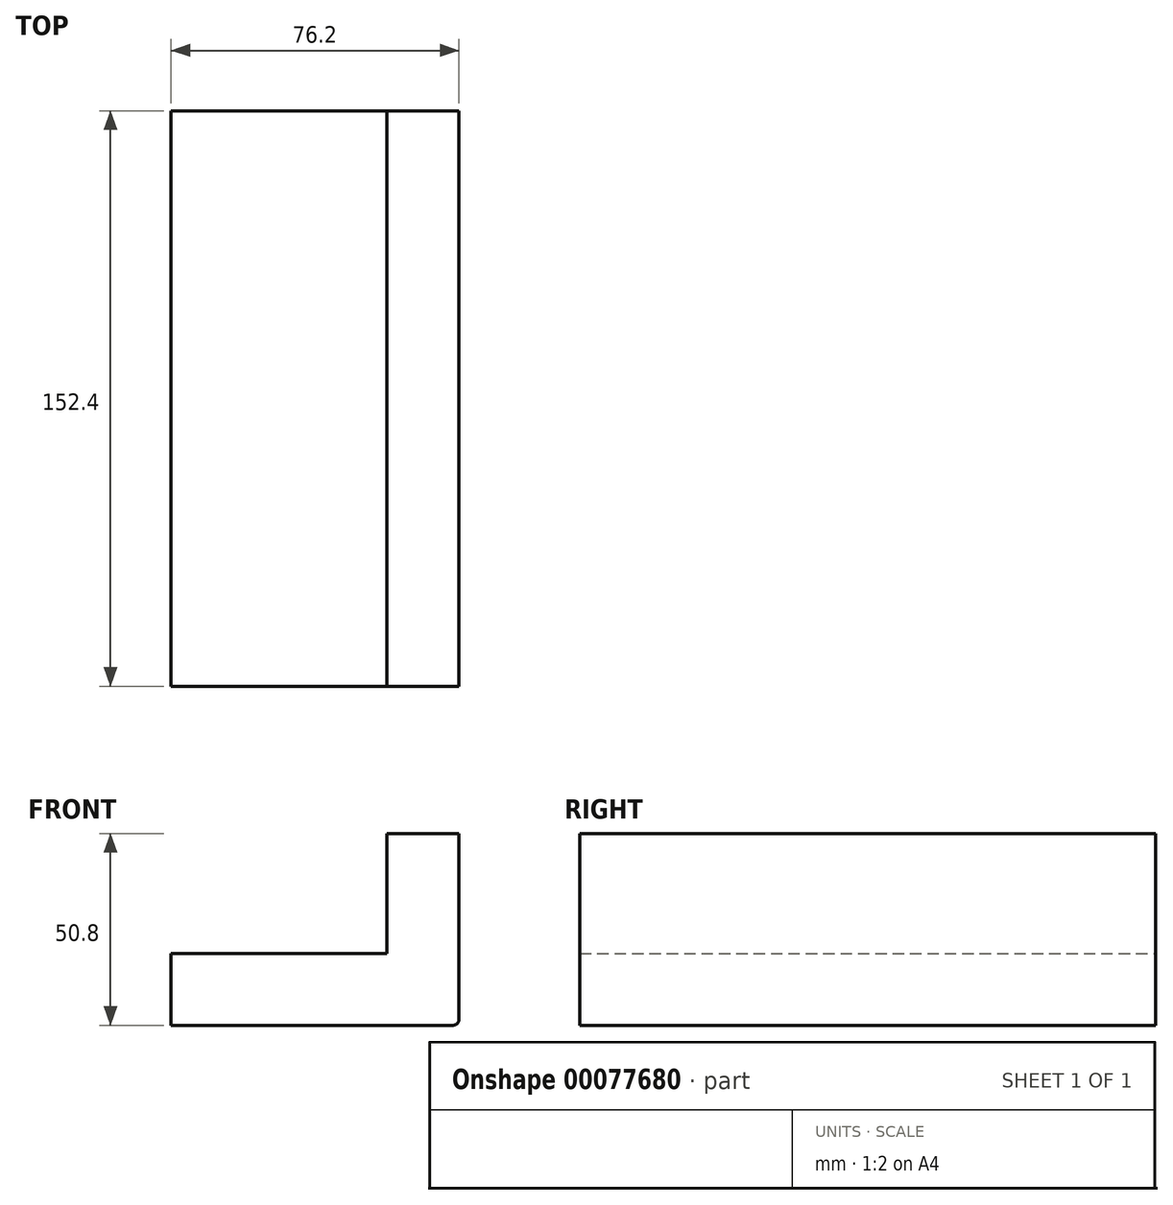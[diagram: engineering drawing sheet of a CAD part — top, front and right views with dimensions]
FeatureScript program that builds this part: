
annotation { "Feature Type Name" : "Feature", "Feature Type Description" : "" }
export const myFeature = defineFeature(function(context is Context, id is Id, definition is map)
    precondition{}
    {
        {
            var Q0;
            Q0=qCreatedBy(makeId("Front.planeOp"),FACE);
            var sketch = newSketch(context, id + "F0", { "sketchPlane" : qUnion([Q0])});
            skLineSegment(sketch, "E0", {"start": v(38.1, -23.81) * mm, "end": v(38.1, 25.4) * mm});
            skLineSegment(sketch, "E1", {"start": v(19.05, -25.4) * mm, "end": v(36.51, -25.4) * mm});
            skLineSegment(sketch, "E2", {"start": v(19.05, 25.4) * mm, "end": v(19.05, -25.4) * mm});
            skLineSegment(sketch, "E3", {"start": v(38.1, 25.4) * mm, "end": v(19.05, 25.4) * mm});
            skLineSegment(sketch, "E4", {"start": v(19.05, -6.35) * mm, "end": v(-38.1, -6.35) * mm});
            skLineSegment(sketch, "E5", {"start": v(-38.1, -6.35) * mm, "end": v(-38.1, -25.4) * mm});
            skLineSegment(sketch, "E6", {"start": v(-38.1, -25.4) * mm, "end": v(19.05, -25.4) * mm});
            skLineSegment(sketch, "E7", {"start": v(19.05, -25.4) * mm, "end": v(19.05, -6.35) * mm});
            skArc(sketch, "E8", {"start": v(36.51, -25.4) * mm, "mid": v(37.64, -24.94) * mm, "end": v(38.1, -23.81) * mm});
            skSolve(sketch);
        }
        {
            var Q0;
            Q0=makeQuery(id+"F0.imprint","IMPRINT",FACE,{"disambiguationData":[TD([[makeQuery(id+"F0.imprint","IMPRINT",EDGE,{"derivedFrom":sQuery(id+"F0.wireOp",EDGE,"E4")}),1.0]])]});
            var Q1;
            Q1=makeQuery(id+"F0.imprint","IMPRINT",FACE,{"disambiguationData":[TD([[makeQuery(id+"F0.imprint","IMPRINT",EDGE,{"derivedFrom":sQuery(id+"F0.wireOp",EDGE,"E0")}),1.0]])]});
            extrude(context, id + "F1", {"entities" : qUnion([Q0, Q1]), "depth" : 152.4 * mm});
        }
    });
